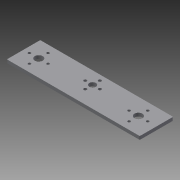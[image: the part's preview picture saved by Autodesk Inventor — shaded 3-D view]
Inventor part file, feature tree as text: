
AUTODESK INVENTOR PART (.ipt)
format: ipt  version: 2014 SP1 (Build 180222100, 222)  size: 107,008 bytes
history: native  units: mm
features: fillet x4, extrude x1, sketch x1
ambient origin geometry x8: Origin, YZ Plane, XZ Plane, XY Plane, X Axis, Y Axis, Z Axis, Center Point
bodies: Solid1 (feature_tree)
feature tree (6):
  extrude  "Extrusion1"  Depth=1.0mm
  fillet  "Fillet1"  Radius=1.0mm
  fillet  "Fillet2"  Radius=1.0mm
  fillet  "Fillet3"  Radius=1.0mm
  fillet  "Fillet4"  [1 undecoded]
  sketch  "Sketch1"  dims[d0=5.0mm d1=0.0mm d2=1.0mm d3=1.0mm d4=1.0mm d5=1.0mm]
note: 1 required parameter value undecoded (feature->parameter linkage not recoverable at this tier; creation-order binding heuristic only, values carry confidence <= 0.55)
